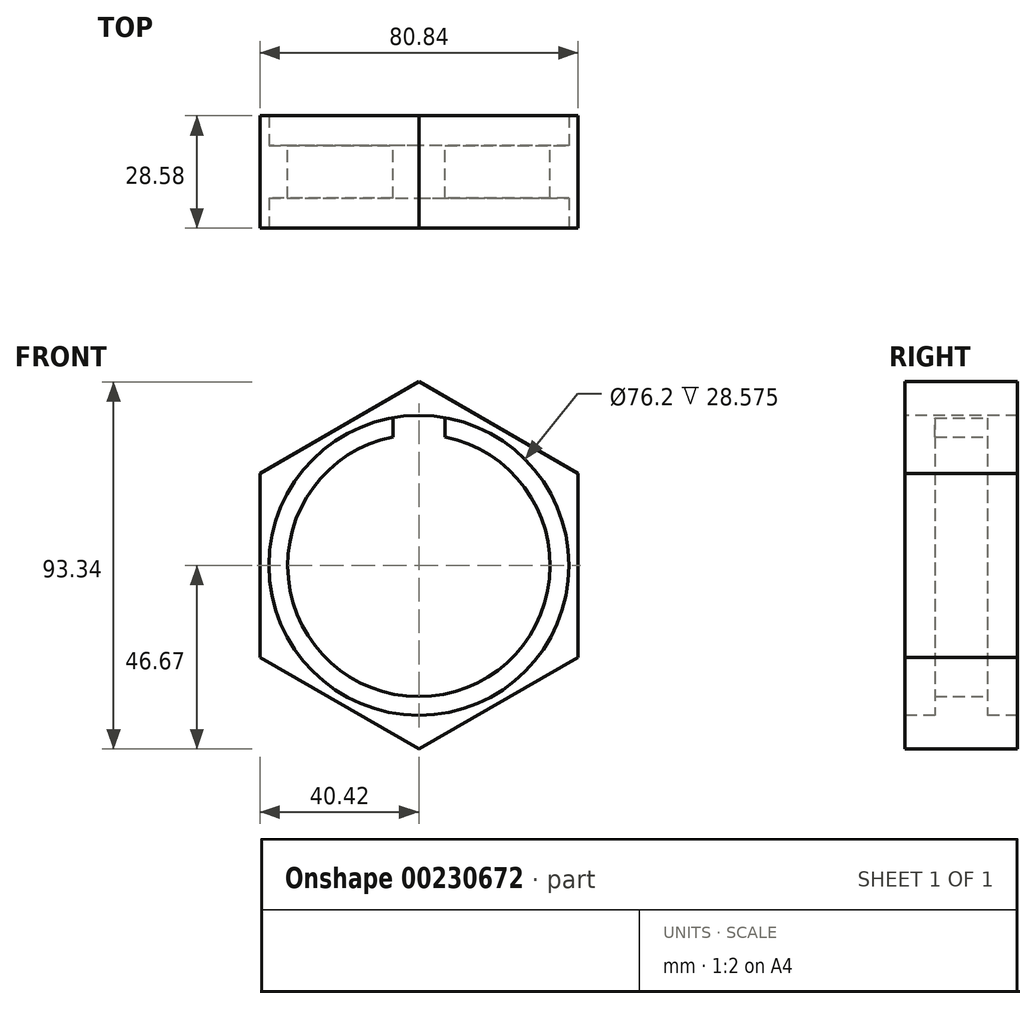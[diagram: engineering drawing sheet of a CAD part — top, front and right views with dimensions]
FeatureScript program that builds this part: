
annotation { "Feature Type Name" : "Feature", "Feature Type Description" : "" }
export const myFeature = defineFeature(function(context is Context, id is Id, definition is map)
    precondition{}
    {
        {
            var Q0;
            Q0=qCreatedBy(makeId("Front.planeOp"),FACE);
            var sketch = newSketch(context, id + "F0", { "sketchPlane" : qUnion([Q0])});
            skCircle(sketch, "E0.cCircle", {"center": v(0, 0) * mm, "radius": 62.23 * mm, "construction": true});
            skLineSegment(sketch, "E0.0", {"start": v(0, 62.23) * mm, "end": v(53.9, 31.12) * mm});
            skLineSegment(sketch, "E0.1", {"start": v(53.9, 31.12) * mm, "end": v(53.9, -31.11) * mm});
            skLineSegment(sketch, "E0.2", {"start": v(53.9, -31.11) * mm, "end": v(0, -62.23) * mm});
            skLineSegment(sketch, "E0.3", {"start": v(0, -62.23) * mm, "end": v(-53.9, -31.12) * mm});
            skLineSegment(sketch, "E0.4", {"start": v(-53.9, -31.12) * mm, "end": v(-53.9, 31.11) * mm});
            skLineSegment(sketch, "E0.5", {"start": v(-53.9, 31.11) * mm, "end": v(0, 62.23) * mm});
            skCircle(sketch, "E1", {"center": v(0, 0) * mm, "radius": 44.45 * mm});
            skSolve(sketch);
        }
        {
            var Q0;
            Q0 = qSketchRegion(id + "F0", true);
            extrude(context, id + "F1", {"entities" : qUnion([Q0]), "depth" : 38.1 * mm});
        }
        {
            var Q0;
            Q0=makeQuery(id+"F1.opExtrude","CAP_FACE",FACE,{"disambiguationData":[OSD([sQuery(id+"F0.wireOp",EDGE,"E0.0"),sQuery(id+"F0.wireOp",EDGE,"E0.1"),sQuery(id+"F0.wireOp",EDGE,"E0.2"),sQuery(id+"F0.wireOp",EDGE,"E0.3"),sQuery(id+"F0.wireOp",EDGE,"E0.4"),sQuery(id+"F0.wireOp",EDGE,"E0.5"),sQuery(id+"F0.wireOp",EDGE,"E1")])],"isStart":false});
            var sketch = newSketch(context, id + "F2", { "sketchPlane" : qUnion([Q0])});
            skCircle(sketch, "E2", {"center": v(0, 0) * mm, "radius": 50.8 * mm});
            skSolve(sketch);
        }
        {
            var Q0;
            Q0 = qSketchRegion(id + "F2", true);
            extrude(context, id + "F3", {"entities" : qUnion([Q0]), "operationType" : NewBodyOperationType.REMOVE, "oppositeDirection" : true, "depth" : 10.16 * mm});
        }
        {
            var Q0;
            Q0=makeQuery(id+"F1.opExtrude","CAP_FACE",FACE,{"disambiguationData":[OSD([sQuery(id+"F0.wireOp",EDGE,"E0.0"),sQuery(id+"F0.wireOp",EDGE,"E0.1"),sQuery(id+"F0.wireOp",EDGE,"E0.2"),sQuery(id+"F0.wireOp",EDGE,"E0.3"),sQuery(id+"F0.wireOp",EDGE,"E0.4"),sQuery(id+"F0.wireOp",EDGE,"E0.5"),sQuery(id+"F0.wireOp",EDGE,"E1")])],"isStart":true});
            var sketch = newSketch(context, id + "F4", { "sketchPlane" : qUnion([Q0])});
            skCircle(sketch, "E3", {"center": v(0, 0) * mm, "radius": 50.8 * mm});
            skSolve(sketch);
        }
        {
            var Q0;
            Q0 = qSketchRegion(id + "F4", true);
            extrude(context, id + "F5", {"entities" : qUnion([Q0]), "operationType" : NewBodyOperationType.REMOVE, "oppositeDirection" : true, "depth" : 10.16 * mm});
        }
        {
            var Q0;
            Q0=makeQuery(id+"F5.boolean.opBoolean","COPY",FACE,{"derivedFrom":makeQuery(id+"F5.opExtrude","CAP_FACE",FACE,{"disambiguationData":[OSD([sQuery(id+"F4.wireOp",EDGE,"E3")])],"isStart":false})});
            var sketch = newSketch(context, id + "F6", { "sketchPlane" : qUnion([Q0])});
            skCircle(sketch, "E4", {"center": v(0, 0) * mm, "radius": 50.8 * mm});
            skCircle(sketch, "E5", {"center": v(0, 0) * mm, "radius": 44.45 * mm});
            skLineSegment(sketch, "E6", {"start": v(0, 0) * mm, "end": v(-8.82, 50.03) * mm});
            skLineSegment(sketch, "E7", {"start": v(0, 0) * mm, "end": v(8.82, 50.03) * mm});
            skLineSegment(sketch, "E8", {"start": v(-8.82, 50.03) * mm, "end": v(-8.82, 0) * mm});
            skLineSegment(sketch, "E9", {"start": v(8.82, 50.03) * mm, "end": v(8.82, 0) * mm});
            skSolve(sketch);
        }
        {
            var Q0;
            {var subQ0=sQuery(id+"F6.wireOp",EDGE,"E6");var subQ5=sQuery(id+"F6.wireOp",EDGE,"E5");var subQ6=makeQuery(id+"F6.imprint","INTERSECT",VERTEX,{"derivedFrom":[subQ5,subQ0]});Q0=makeQuery(id+"F6.imprint","IMPRINT",FACE,{"disambiguationData":[TD([[makeQuery(id+"F6.imprint","IMPRINT",EDGE,{"disambiguationData":[TD([[subQ6,1.0]])],"derivedFrom":subQ5}),-1.0]])]});}
            var Q1;
            {var subQ0=sQuery(id+"F6.wireOp",EDGE,"E8");var subQ1=sQuery(id+"F6.wireOp",EDGE,"E5");var subQ2=makeQuery(id+"F6.imprint","INTERSECT",VERTEX,{"derivedFrom":[subQ1,subQ0]});Q1=makeQuery(id+"F6.imprint","IMPRINT",FACE,{"disambiguationData":[TD([[makeQuery(id+"F6.imprint","IMPRINT",EDGE,{"disambiguationData":[TD([[subQ2,1.0]])],"derivedFrom":subQ1}),-1.0]])]});}
            var Q2;
            {var subQ0=sQuery(id+"F6.wireOp",EDGE,"E9");var subQ1=sQuery(id+"F6.wireOp",EDGE,"E5");var subQ2=makeQuery(id+"F6.imprint","INTERSECT",VERTEX,{"derivedFrom":[subQ1,subQ0]});Q2=makeQuery(id+"F6.imprint","IMPRINT",FACE,{"disambiguationData":[TD([[makeQuery(id+"F6.imprint","IMPRINT",EDGE,{"disambiguationData":[TD([[subQ2,-1.0]])],"derivedFrom":subQ1}),-1.0]])]});}
            extrude(context, id + "F7", {"entities" : qUnion([Q0, Q1, Q2]), "operationType" : NewBodyOperationType.REMOVE, "oppositeDirection" : true, "depth" : 25.4 * mm});
        }
        {
            var Q0;
            Q0=makeQuery(id+"F1.opExtrude","SWEPT_BODY",BODY,{"disambiguationData":[OSD([sQuery(id+"F0.wireOp",EDGE,"E0.0"),sQuery(id+"F0.wireOp",EDGE,"E0.1"),sQuery(id+"F0.wireOp",EDGE,"E0.2"),sQuery(id+"F0.wireOp",EDGE,"E0.3"),sQuery(id+"F0.wireOp",EDGE,"E0.4"),sQuery(id+"F0.wireOp",EDGE,"E0.5"),sQuery(id+"F0.wireOp",EDGE,"E1")])]});
            var Q1;
            Q1=sQuery(id+"F0.wireOp",VERTEX,"E0.cCircle.center");
            transform(context, id + "F8", {"entities" : qUnion([Q0]), "transformType" : TransformType.SCALE_UNIFORMLY, "scale" : .75, "scalePoint" : qUnion([Q1]), "makeCopy" : false});
        }
    });
